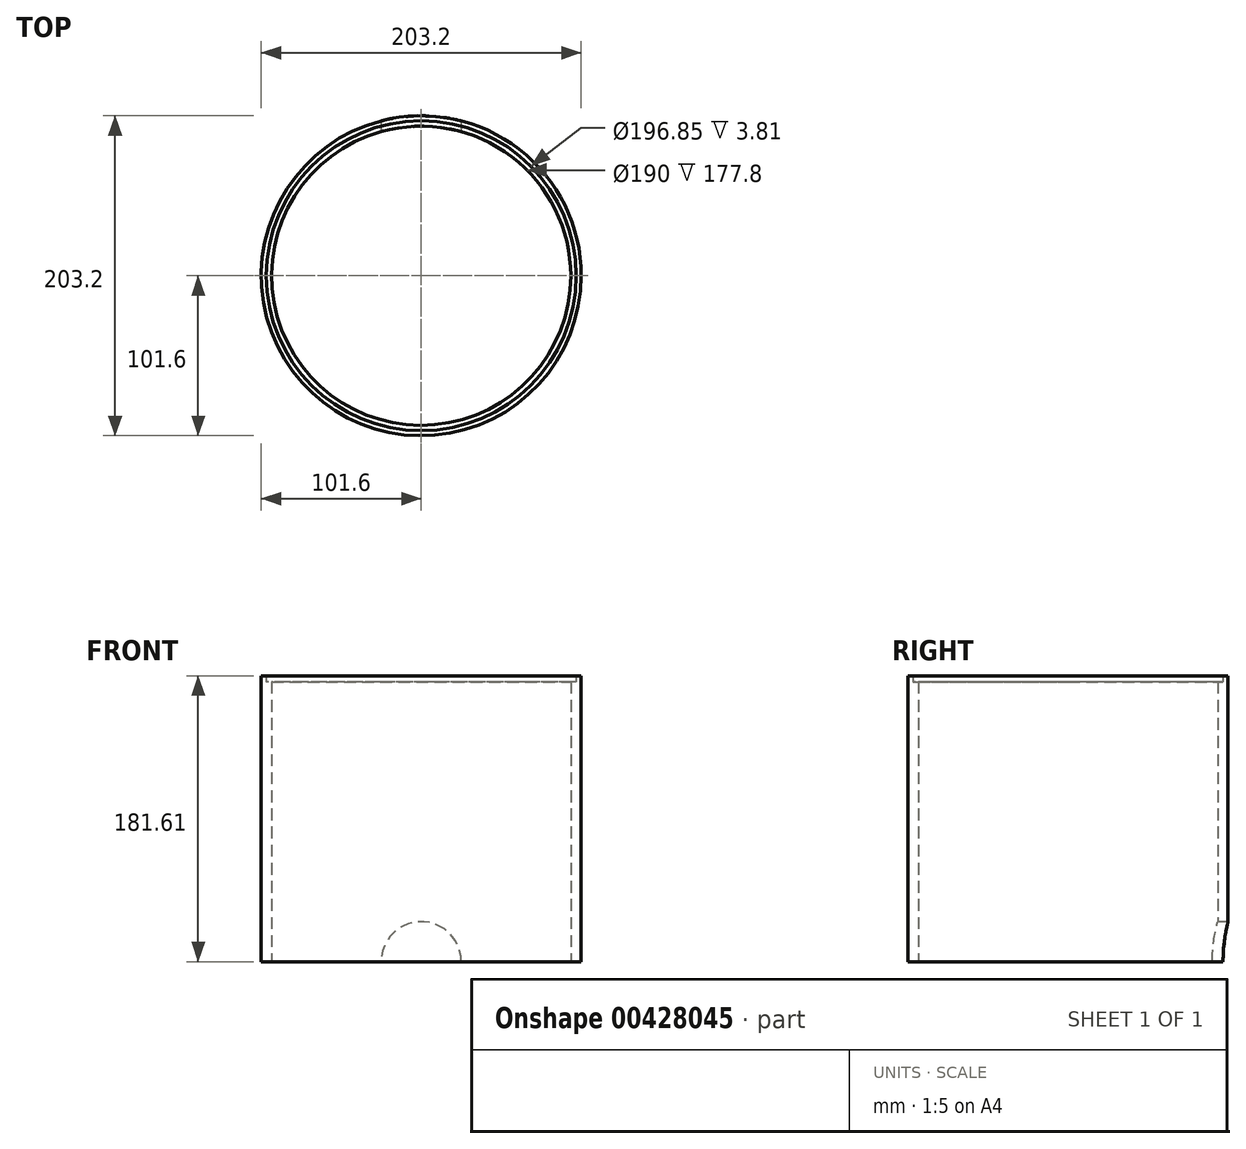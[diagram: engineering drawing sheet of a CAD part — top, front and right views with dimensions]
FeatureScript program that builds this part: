
annotation { "Feature Type Name" : "Feature", "Feature Type Description" : "" }
export const myFeature = defineFeature(function(context is Context, id is Id, definition is map)
    precondition{}
    {
        {
            var Q0;
            Q0=qCreatedBy(makeId("Top.planeOp"),FACE);
            var sketch = newSketch(context, id + "F0", { "sketchPlane" : qUnion([Q0])});
            skCircle(sketch, "E0", {"center": v(0, 0) * mm, "radius": 98.43 * mm});
            skCircle(sketch, "E1", {"center": v(0, 0) * mm, "radius": 95 * mm});
            skCircle(sketch, "E2", {"center": v(0, 0) * mm, "radius": 101.6 * mm});
            skSolve(sketch);
        }
        {
            var Q0;
            Q0=makeQuery(id+"F0.imprint","IMPRINT",FACE,{"disambiguationData":[TD([[makeQuery(id+"F0.imprint","IMPRINT",EDGE,{"derivedFrom":sQuery(id+"F0.wireOp",EDGE,"E0")}),-1.0]])]});
            extrude(context, id + "F1", {"entities" : qUnion([Q0]), "depth" : 181.6 * mm});
        }
        {
            var Q0;
            Q0=makeQuery(id+"F0.imprint","IMPRINT",FACE,{"disambiguationData":[TD([[makeQuery(id+"F0.imprint","IMPRINT",EDGE,{"derivedFrom":sQuery(id+"F0.wireOp",EDGE,"E0")}),1.0]])]});
            extrude(context, id + "F2", {"entities" : qUnion([Q0]), "operationType" : NewBodyOperationType.ADD, "depth" : 177.8 * mm, "hasSecondDirection" : true, "secondDirectionOppositeDirection" : false, "secondDirectionDepth" : 0 * mm});
        }
        {
            var Q0;
            Q0=qCreatedBy(makeId("Front.planeOp"),FACE);
            var sketch = newSketch(context, id + "F3", { "sketchPlane" : qUnion([Q0])});
            skCircle(sketch, "E3", {"center": v(0, 0) * mm, "radius": 25.4 * mm});
            skLineSegment(sketch, "E4", {"start": v(0, 0) * mm, "end": v(0, -61.5) * mm});
            skSolve(sketch);
        }
        {
            var Q0;
            Q0=makeQuery(id+"F3.imprint","IMPRINT",FACE,{"disambiguationData":[TD([[makeQuery(id+"F3.imprint","IMPRINT",EDGE,{"derivedFrom":sQuery(id+"F3.wireOp",EDGE,"E3")}),1.0]])]});
            extrude(context, id + "F4", {"entities" : qUnion([Q0]), "operationType" : NewBodyOperationType.REMOVE, "endBound" : BoundingType.THROUGH_ALL, "oppositeDirection" : true, "depth" : 203.2 * mm});
        }
    });
